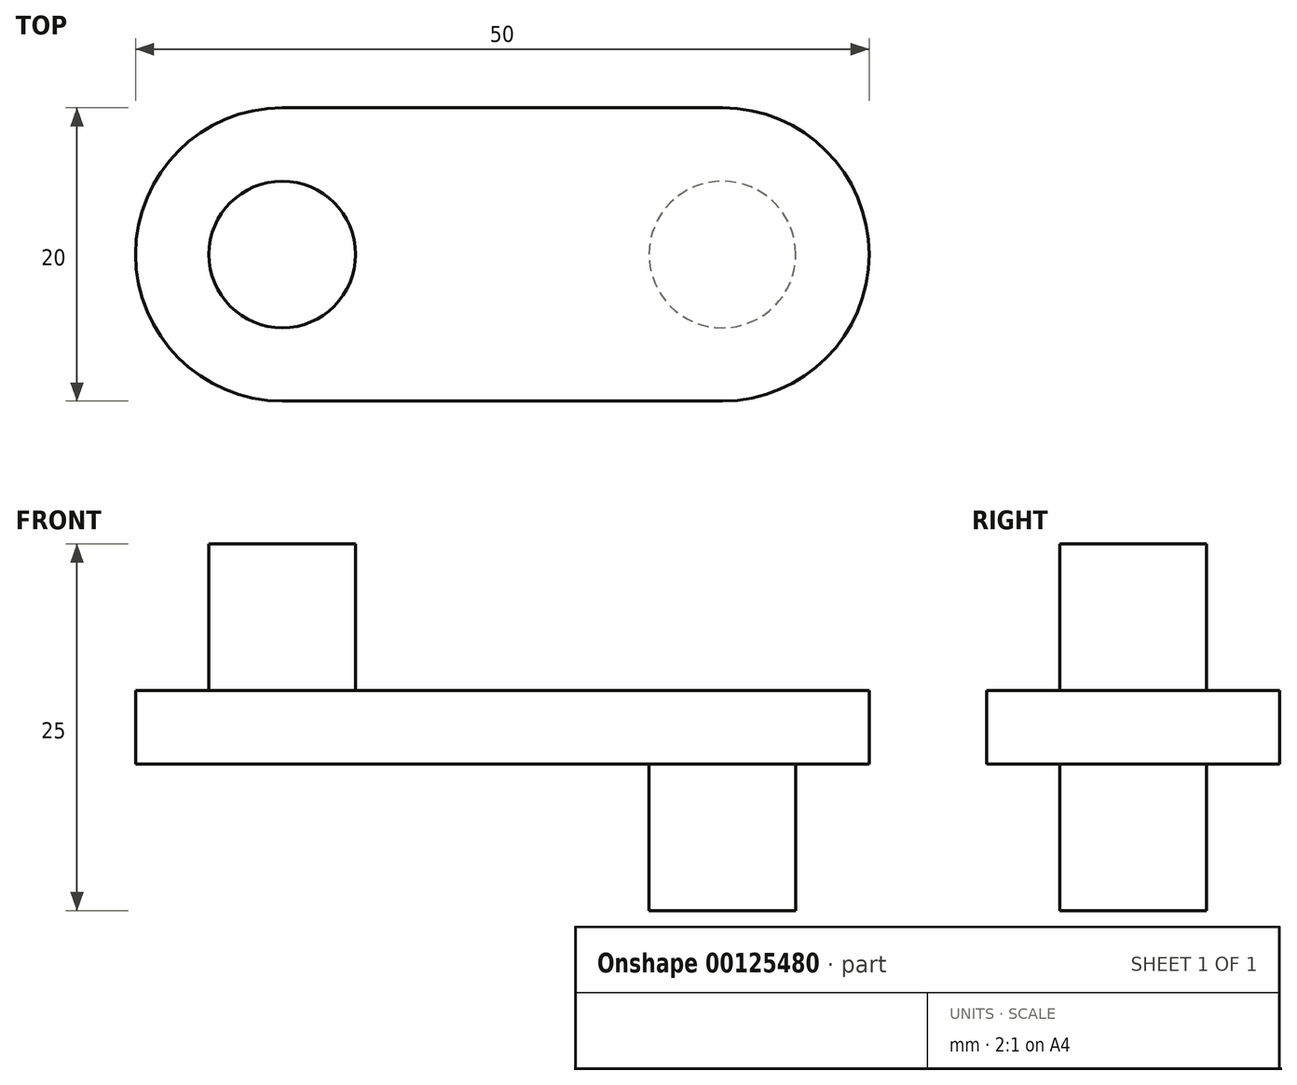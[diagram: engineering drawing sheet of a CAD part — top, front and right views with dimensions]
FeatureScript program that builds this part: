
annotation { "Feature Type Name" : "Feature", "Feature Type Description" : "" }
export const myFeature = defineFeature(function(context is Context, id is Id, definition is map)
    precondition{}
    {
        {
            var Q0;
            Q0=qCreatedBy(makeId("Top.planeOp"),FACE);
            var sketch = newSketch(context, id + "F0", { "sketchPlane" : qUnion([Q0])});
            skLineSegment(sketch, "E0", {"start": v(0, 0) * mm, "end": v(30, 0) * mm});
            skLineSegment(sketch, "E1", {"start": v(0, 20) * mm, "end": v(30, 20) * mm});
            skArc(sketch, "E2", {"start": v(0, 20) * mm, "mid": v(-10, 10) * mm, "end": v(0, 0) * mm});
            skArc(sketch, "E3", {"start": v(30, 0) * mm, "mid": v(40, 10) * mm, "end": v(30, 20) * mm});
            skSolve(sketch);
        }
        {
            var Q0;
            Q0 = qSketchRegion(id + "F0", true);
            extrude(context, id + "F1", {"entities" : qUnion([Q0]), "depth" : 5 * mm});
        }
        {
            var Q0;
            Q0=qCreatedBy(makeId("Top.planeOp"),FACE);
            var sketch = newSketch(context, id + "F2", { "sketchPlane" : qUnion([Q0])});
            skCircle(sketch, "E4", {"center": v(0, 10) * mm, "radius": 5 * mm});
            skSolve(sketch);
        }
        {
            var Q0;
            Q0 = qSketchRegion(id + "F2", true);
            extrude(context, id + "F3", {"entities" : qUnion([Q0]), "operationType" : NewBodyOperationType.ADD, "depth" : 15 * mm});
        }
        {
            var Q0;
            Q0=qCreatedBy(makeId("Top.planeOp"),FACE);
            var sketch = newSketch(context, id + "F4", { "sketchPlane" : qUnion([Q0])});
            skCircle(sketch, "E5", {"center": v(30, 10) * mm, "radius": 5 * mm});
            skSolve(sketch);
        }
        {
            var Q0;
            Q0 = qSketchRegion(id + "F4", true);
            extrude(context, id + "F5", {"entities" : qUnion([Q0]), "operationType" : NewBodyOperationType.ADD, "oppositeDirection" : true, "depth" : 10 * mm});
        }
    });
